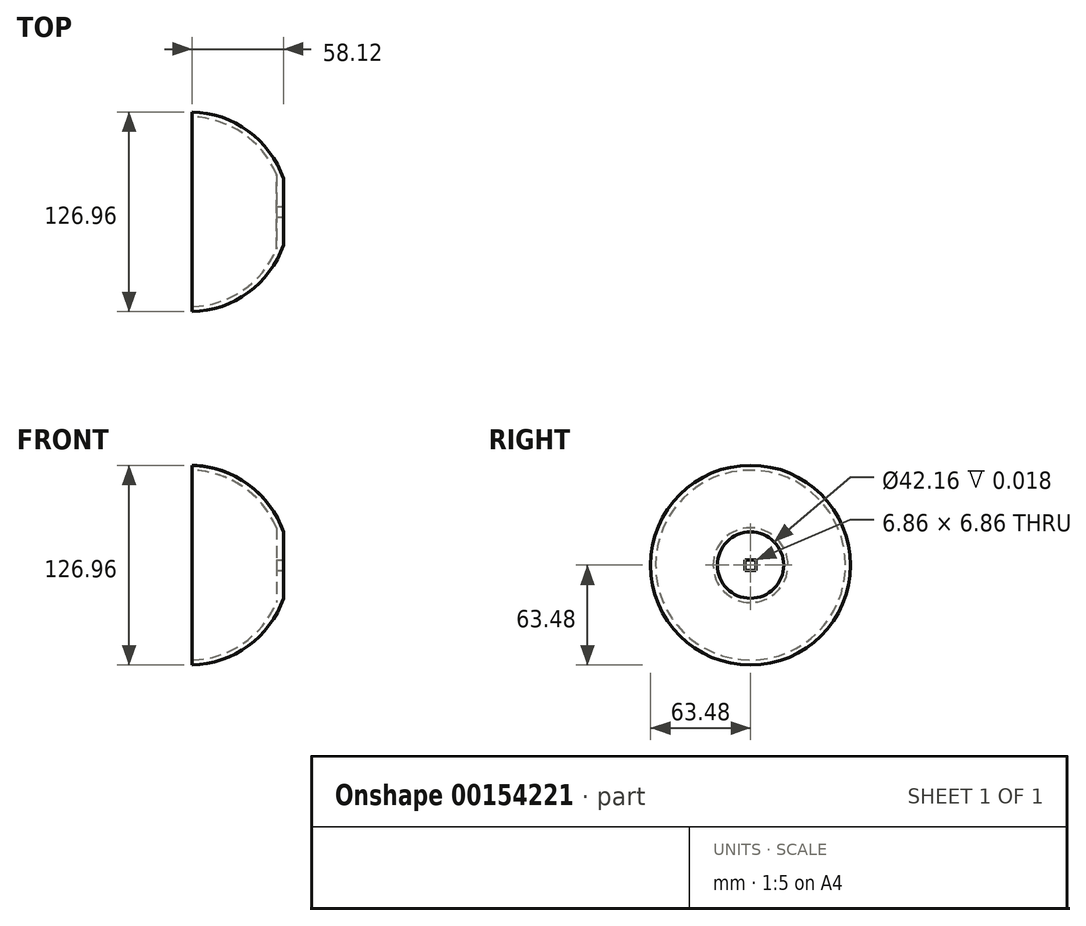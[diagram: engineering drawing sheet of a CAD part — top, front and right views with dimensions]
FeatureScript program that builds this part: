
annotation { "Feature Type Name" : "Feature", "Feature Type Description" : "" }
export const myFeature = defineFeature(function(context is Context, id is Id, definition is map)
    precondition{}
    {
        {
            var Q0;
            Q0=qCreatedBy(makeId("Front.planeOp"),FACE);
            var sketch = newSketch(context, id + "F0", { "sketchPlane" : qUnion([Q0])});
            skCircle(sketch, "E0", {"center": v(0, 0) * mm, "radius": 63.5 * mm});
            skCircle(sketch, "E1", {"center": v(0, 0) * mm, "radius": 60.33 * mm});
            skLineSegment(sketch, "E2", {"start": v(0, 63.5) * mm, "end": v(0, -63.5) * mm, "construction": true});
            skLineSegment(sketch, "E3", {"start": v(1.78, 71.34) * mm, "end": v(1.78, -81.57) * mm});
            skLineSegment(sketch, "E4", {"start": v(1.78, 0) * mm, "end": v(63.5, 0) * mm});
            skLineSegment(sketch, "E5", {"start": v(55.46, 23.73) * mm, "end": v(55.46, 0) * mm});
            skSolve(sketch);
        }
        {
            var Q0;
            {var subQ0=sQuery(id+"F0.wireOp",EDGE,"E4");var subQ1=sQuery(id+"F0.wireOp",EDGE,"E0");var subQ2=makeQuery(id+"F0.imprint","INTERSECT",VERTEX,{"derivedFrom":[subQ1,subQ0]});Q0=makeQuery(id+"F0.imprint","IMPRINT",FACE,{"disambiguationData":[TD([[makeQuery(id+"F0.imprint","IMPRINT",EDGE,{"disambiguationData":[TD([[subQ2,-1.0]])],"derivedFrom":subQ1}),1.0]])]});}
            var Q1;
            {var subQ0=sQuery(id+"F0.wireOp",EDGE,"E5");Q1=makeQuery(id+"F0.imprint","IMPRINT",FACE,{"disambiguationData":[TD([[makeQuery(id+"F0.imprint","IMPRINT",EDGE,{"derivedFrom":subQ0}),1.0]])]});}
            var Q2;
            Q2=sQuery(id+"F0.wireOp",EDGE,"E4");
            revolve(context, id + "F1", {"entities" : qUnion([Q0, Q1]), "axis" : qUnion([Q2]), "revolveType" : RevolveType.FULL});
        }
        {
            var Q0;
            Q0=qCreatedBy(makeId("Right.planeOp"),FACE);
            cPlane(context, id + "F2", {"entities" : qUnion([Q0]), "cplaneType" : CPlaneType.OFFSET, "offset" : 76.2 * mm, "width" : 152.4 * mm, "height" : 152.4 * mm});
        }
        {
            var Q0;
            Q0=qCreatedBy(id+"F2.planeOp",FACE);
            var sketch = newSketch(context, id + "F3", { "sketchPlane" : qUnion([Q0])});
            skCircle(sketch, "E6", {"center": v(0, 0) * mm, "radius": 21.08 * mm});
            skLineSegment(sketch, "E7.bottom", {"start": v(3.43, 3.43) * mm, "end": v(-3.43, 3.43) * mm});
            skLineSegment(sketch, "E7.top", {"start": v(3.43, -3.43) * mm, "end": v(-3.43, -3.43) * mm});
            skLineSegment(sketch, "E7.left", {"start": v(3.43, 3.43) * mm, "end": v(3.43, -3.43) * mm});
            skLineSegment(sketch, "E7.right", {"start": v(-3.43, 3.43) * mm, "end": v(-3.43, -3.43) * mm});
            skSolve(sketch);
        }
        {
            var Q0;
            Q0=makeQuery(id+"F3.imprint","IMPRINT",FACE,{"disambiguationData":[TD([[makeQuery(id+"F3.imprint","IMPRINT",EDGE,{"derivedFrom":sQuery(id+"F3.wireOp",EDGE,"E6")}),1.0]])]});
            extrude(context, id + "F4", {"entities" : qUnion([Q0]), "operationType" : NewBodyOperationType.REMOVE, "oppositeDirection" : true, "depth" : 16.32 * mm});
        }
        {
            var Q0;
            Q0=makeQuery(id+"F3.imprint","IMPRINT",FACE,{"disambiguationData":[TD([[makeQuery(id+"F3.imprint","IMPRINT",EDGE,{"derivedFrom":sQuery(id+"F3.wireOp",EDGE,"E7.bottom")}),1.0]])]});
            extrude(context, id + "F5", {"entities" : qUnion([Q0]), "operationType" : NewBodyOperationType.REMOVE, "oppositeDirection" : true, "depth" : 54.36 * mm});
        }
    });
